FCSTD DOCUMENT  (FreeCAD 0.18R16268 (Git))
Label: asm_Bielle
License: All rights reserved
LicenseURL: http://en.wikipedia.org/wiki/All_rights_reserved
objects: App::Link×5, App::FeaturePython×5, PartDesign::CoordinateSystem×2, App::DocumentObjectGroup×1, App::Part×1
note: 2 computed .brp shape members not serialized (recipe doc carries the construction recipe); baked Part::Feature solids carry a one-line shape summary decoded from their .brp
EXTERNAL_REF file=Bielle.fcstd obj=Model
EXTERNAL_REF file=Cuve.fcstd obj=Model
EXTERNAL_REF file=Bague.fcstd obj=Model
EXTERNAL_REF file=Screw_CHC.fcstd obj=Model

FEATURE [PartDesign::CoordinateSystem] LCS_0
  AttacherType = Attacher::AttachEngine3D
FEATURE [App::Link] Bielle
  LinkedObject = -> <external Bielle.fcstd>#Model
  expr: Placement = <<LCS_0>>.Placement.multiply(<<constr_Bielle>>.AttachmentOffset).multiply(.<<LCS_0.>>.Placement.inverse())
FEATURE [App::FeaturePython] constr_Bielle  # WARN: FeaturePython — macro-defined, semantics opaque (R4)
  AttachedTo = Parent Assembly
  AttachmentLCS = LCS_0
  Link_Name = Bielle
  LinkedPartLCS = LCS_0
  Linked_File = Bielle
FEATURE [App::Link] Cuve
  LinkPlacement = pos=(125,0,0) rot=(0,0,1;0rad)
  LinkedObject = -> <external Cuve.fcstd>#Model
  Placement = pos=(125,0,0) rot=(0,0,1;0rad)
  expr: Placement = <<Bielle>>.Placement.multiply(<<Bielle>>.<<LCS_1.>>.Placement).multiply(<<constr_Cuve>>.AttachmentOffset).multiply(.<<LCS_0.>>.Placement.inverse())
FEATURE [App::FeaturePython] constr_Cuve  # WARN: FeaturePython — macro-defined, semantics opaque (R4)
  AttachedTo = Bielle
  AttachmentLCS = LCS_1
  Link_Name = Cuve
  LinkedPartLCS = LCS_0
  Linked_File = Cuve
FEATURE [App::Link] Bague
  LinkPlacement = pos=(0,0,-15) rot=(0,0,1;0rad)
  LinkedObject = -> <external Bague.fcstd>#Model
  Placement = pos=(0,0,-15) rot=(0,0,1;0rad)
  expr: Placement = <<Bielle>>.Placement.multiply(<<Bielle>>.<<LCS_0.>>.Placement).multiply(<<constr_Bague>>.AttachmentOffset).multiply(.<<LCS_0.>>.Placement.inverse())
FEATURE [App::FeaturePython] constr_Bague  # WARN: FeaturePython — macro-defined, semantics opaque (R4)
  AttachedTo = Bielle
  AttachmentLCS = LCS_0
  AttachmentOffset = pos=(0,0,-15) rot=(0,0,1;0rad)
  Link_Name = Bague
  LinkedPartLCS = LCS_0
  Linked_File = Bague
FEATURE [App::Link] Screw_CHC_1
  LinkPlacement = pos=(130,-32.5,-1.7e-14) rot=(0.707107,0,0.707107;3.14159rad)
  LinkedObject = -> <external Screw_CHC.fcstd>#Model
  Placement = pos=(130,-32.5,-1.7e-14) rot=(0.707107,0,0.707107;3.14159rad)
  expr: Placement = <<Cuve>>.Placement.multiply(<<Cuve>>.<<LCS_1.>>.Placement).multiply(<<constr_Screw_CHC_1>>.AttachmentOffset).multiply(.<<LCS_0.>>.Placement.inverse())
FEATURE [App::FeaturePython] constr_Screw_CHC_1  # WARN: FeaturePython — macro-defined, semantics opaque (R4)
  AttachedTo = Cuve
  AttachmentLCS = LCS_1
  Link_Name = Screw_CHC_1
  LinkedPartLCS = LCS_0
  Linked_File = Screw_CHC
FEATURE [App::Link] Screw_CHC_2
  LinkPlacement = pos=(130,32.5,-2.6e-15) rot=(0.707107,0,0.707107;3.14159rad)
  LinkedObject = -> <external Screw_CHC.fcstd>#Model
  Placement = pos=(130,32.5,-2.6e-15) rot=(0.707107,0,0.707107;3.14159rad)
  expr: Placement = <<Cuve>>.Placement.multiply(<<Cuve>>.<<LCS_2.>>.Placement).multiply(<<constr_Screw_CHC_2>>.AttachmentOffset).multiply(.<<LCS_0.>>.Placement.inverse())
FEATURE [App::FeaturePython] constr_Screw_CHC_2  # WARN: FeaturePython — macro-defined, semantics opaque (R4)
  AttachedTo = Cuve
  AttachmentLCS = LCS_2
  Link_Name = Screw_CHC_2
  LinkedPartLCS = LCS_0
  Linked_File = Screw_CHC
FEATURE [App::DocumentObjectGroup] Constraints
  Group = -> [constr_Bielle,constr_Cuve,constr_Bague,constr_Screw_CHC_1,constr_Screw_CHC_2]
FEATURE [PartDesign::CoordinateSystem] LCS_Cuve
  AttacherType = Attacher::AttachEngine3D
  Placement = pos=(125,0,0) rot=(0,0,1;0rad)
  expr: Placement = <<Cuve>>.Placement.multiply(<<Cuve>>.<<LCS_0.>>.Placement)
FEATURE [App::Part] Model
  Group = -> [Constraints,LCS_0,Bielle,constr_Bielle,Cuve,constr_Cuve,Bague,constr_Bague,Screw_CHC_1,constr_Screw_CHC_1,Screw_CHC_2,constr_Screw_CHC_2,LCS_Cuve]
  Origin = -> Origin

RESOLVED EXTERNAL PARTS (link-assembly join: the EXTERNAL_REF files above that resolve inside this repo's crawl, each included once):
---- part Bague.fcstd = doc fcstd_d0fe9226a57d ----
FCSTD DOCUMENT  (FreeCAD 0.18R16268 (Git))
Label: Bague
License: All rights reserved
LicenseURL: http://en.wikipedia.org/wiki/All_rights_reserved
objects: PartDesign::CoordinateSystem×3, App::DocumentObjectGroup×1, Sketcher::SketchObject×1, PartDesign::Pad×1, PartDesign::Chamfer×1, PartDesign::Body×1, App::Part×1
note: 8 computed .brp shape members not serialized (recipe doc carries the construction recipe); baked Part::Feature solids carry a one-line shape summary decoded from their .brp

FEATURE [App::DocumentObjectGroup] Constraints
FEATURE [PartDesign::CoordinateSystem] LCS_0
  AttacherType = Attacher::AttachEngine3D
FEATURE [PartDesign::CoordinateSystem] LCS_001
  AttacherType = Attacher::AttachEngine3D
FEATURE [Sketcher::SketchObject] Sketch
  MapMode = 5
  Support = -> [XY_Plane001]
  sketch-geometry (2):
    g0: Circle CenterX=0 CenterY=0 CenterZ=0 NormalX=0 NormalY=0 NormalZ=1 AngleXU=0 Radius=8
    g1: Circle CenterX=0 CenterY=0 CenterZ=0 NormalX=0 NormalY=0 NormalZ=1 AngleXU=0 Radius=10
  constraints (4):
    c: Coincident(g0,g-1)
    c: Coincident(g1,g0)
    c: Diameter(g1) = 20
    c: Diameter(g0) = 16
FEATURE [PartDesign::Pad] Pad
  ClaimChildren = false
  Length = 30
  Length2 = 100
  Profile = -> Sketch
  Type = 0
FEATURE [PartDesign::Chamfer] Chamfer
  Base = -> Pad [Face4,Face3]
  BaseFeature = -> Pad
  Size = 0.5
FEATURE [PartDesign::Body] Body
  Group = -> [LCS_001,Sketch,Pad,Chamfer]
  Origin = -> Origin001
  Tip = -> Chamfer
FEATURE [PartDesign::CoordinateSystem] LCS_1
  AttacherType = Attacher::AttachEngine3D
  AttachmentOffset = pos=(0,0,0) rot=(0,0,-1;1.5708rad)
  MapMode = 11
  Placement = pos=(0,0,30) rot=(0,0,1;0rad)
  Support = -> [Pad]
FEATURE [App::Part] Model
  Group = -> [Constraints,LCS_0,Body,LCS_1]
  Origin = -> Origin
---- part Bielle.fcstd = doc fcstd_74266f76e503 ----
FCSTD DOCUMENT  (FreeCAD 0.18R16268 (Git))
Label: Bielle
License: All rights reserved
LicenseURL: http://en.wikipedia.org/wiki/All_rights_reserved
objects: Sketcher::SketchObject×6, PartDesign::Pad×3, PartDesign::CoordinateSystem×2, PartDesign::Plane×2, PartDesign::Pocket×2, App::DocumentObjectGroup×1, PartDesign::Mirrored×1, PartDesign::Body×1, App::Part×1
note: 22 computed .brp shape members not serialized (recipe doc carries the construction recipe); baked Part::Feature solids carry a one-line shape summary decoded from their .brp

FEATURE [App::DocumentObjectGroup] Constraints
FEATURE [PartDesign::CoordinateSystem] LCS_0
  AttacherType = Attacher::AttachEngine3D
FEATURE [PartDesign::Plane] DatumPlane
  AttachmentOffset = pos=(0,0,1.5) rot=(0,0,1;0rad)
  Length = 161.166
  MapMode = 5
  Placement = pos=(0,0,1.5) rot=(0,0,1;0rad)
  ResizeMode = 0
  Support = -> [LCS_0]
  Width = 101.166
FEATURE [Sketcher::SketchObject] Sketch  label="Length"
  MapMode = 5
  Support = -> [XY_Plane001]
  sketch-geometry (1):
    g0: LineSegment StartX=0 StartY=0 StartZ=0 EndX=125 EndY=0 EndZ=0
  constraints (3):
    c: Horizontal(g0)
    c: DistanceX(g0,g0) = 125
    c: Coincident(g-1,g0)
FEATURE [PartDesign::Plane] DatumPlane001
  Length = 88.9443
  MapMode = 7
  Placement = pos=(125,0,0) rot=(0.57735,-0.57735,-0.57735;2.0944rad)
  ResizeMode = 0
  Support = -> [Sketch]
  Width = 33.9443
FEATURE [Sketcher::SketchObject] Sketch006
  MapMode = 5
  Placement = pos=(125,0,0) rot=(0.57735,-0.57735,-0.57735;2.0944rad)
  Support = -> [DatumPlane001]
  sketch-geometry (2):
    g0: Circle CenterX=-32.5 CenterY=0 CenterZ=0 NormalX=0 NormalY=0 NormalZ=1 AngleXU=0 Radius=2.5
    g1: Circle CenterX=32.5 CenterY=0 CenterZ=0 NormalX=0 NormalY=0 NormalZ=1 AngleXU=0 Radius=2.5
  constraints (5):
    c: Symmetric(g0,g1,g-2)
    c: PointOnObject(g1,g-1)
    c: Equal(g0,g1)
    c: Diameter(g0) = 5
    c: DistanceX(g0,g1) = 65
FEATURE [Sketcher::SketchObject] Sketch001
  MapMode = 5
  Support = -> [XY_Plane001]
  sketch-geometry (2):
    g0: Circle CenterX=0 CenterY=0 CenterZ=0 NormalX=0 NormalY=0 NormalZ=1 AngleXU=0 Radius=10
    g1: Circle CenterX=0 CenterY=0 CenterZ=0 NormalX=0 NormalY=0 NormalZ=1 AngleXU=0 Radius=15
  constraints (4):
    c: Coincident(g0,g-1)
    c: Diameter(g0) = 20
    c: Diameter(g1) = 30
    c: Coincident(g1,g0)
FEATURE [PartDesign::Pad] Pad
  ClaimChildren = false
  Length = 25
  Length2 = 100
  Midplane = true
  Profile = -> Sketch001
  Type = 0
FEATURE [Sketcher::SketchObject] Sketch003
  ExternalGeometry = -> [Sketch]
  MapMode = 5
  Support = -> [XY_Plane001]
  sketch-geometry (4):
    g0: ArcOfCircle CenterX=125 CenterY=0 CenterZ=0 NormalX=0 NormalY=0 NormalZ=1 AngleXU=0 Radius=20 StartAngle=1.5708 EndAngle=4.71239
    g1: ArcOfCircle CenterX=125 CenterY=0 CenterZ=0 NormalX=0 NormalY=0 NormalZ=1 AngleXU=0 Radius=25 StartAngle=1.5708 EndAngle=4.71239
    g2: LineSegment StartX=125 StartY=25 StartZ=0 EndX=125 EndY=20 EndZ=0
    g3: LineSegment StartX=125 StartY=-20 StartZ=0 EndX=125 EndY=-25 EndZ=0
  constraints (12):
    c: Coincident(g0,g-3)
    c: Coincident(g1,g0)
    c: Coincident(g2,g1)
    c: Coincident(g2,g0)
    c: Coincident(g3,g0)
    c: Coincident(g3,g1)
    c: Vertical(g2)
    c: Vertical(g3)
    c: PointOnObject(g0,g2)
    c: PointOnObject(g0,g3)
    c: DistanceY(g2,g2) = 5
    c: Diameter(g0) = 40
FEATURE [Sketcher::SketchObject] Sketch004
  ExternalGeometry = -> [Sketch001,Sketch003]
  MapMode = 5
  Support = -> [XY_Plane001]
  sketch-geometry (10):
    g0: LineSegment StartX=125 StartY=25 StartZ=0 EndX=125 EndY=40 EndZ=0
    g1: LineSegment StartX=125 StartY=40 StartZ=0 EndX=115 EndY=40 EndZ=0
    g2: LineSegment StartX=115 StartY=40 StartZ=0 EndX=95 EndY=20 EndZ=0
    g3: LineSegment StartX=95 StartY=20 StartZ=0 EndX=11.1803 EndY=10 EndZ=0
    g4: LineSegment StartX=11.1803 StartY=-10 StartZ=0 EndX=95 EndY=-20 EndZ=0
    g5: LineSegment StartX=95 StartY=-20 StartZ=0 EndX=115 EndY=-40 EndZ=0
    g6: LineSegment StartX=115 StartY=-40 StartZ=0 EndX=125 EndY=-40 EndZ=0
    g7: LineSegment StartX=125 StartY=-40 StartZ=0 EndX=125 EndY=-25 EndZ=0
    g8: ArcOfCircle CenterX=125 CenterY=8e-16 CenterZ=0 NormalX=0 NormalY=0 NormalZ=1 AngleXU=0 Radius=25 StartAngle=1.5708 EndAngle=4.71239
    g9: ArcOfCircle CenterX=0 CenterY=-9e-16 CenterZ=0 NormalX=0 NormalY=0 NormalZ=1 AngleXU=0 Radius=15 StartAngle=5.55346 EndAngle=7.01291
  constraints (27):
    c: Coincident(g0,g1)
    c: Coincident(g1,g2)
    c: Coincident(g2,g3)
    c: PointOnObject(g3,g-3)
    c: Coincident(g4,g5)
    c: Coincident(g5,g6)
    c: Coincident(g6,g7)
    c: Coincident(g7,g-4)
    c: Vertical(g0)
    c: Symmetric(g3,g4,g-1)
    c: DistanceY(g4,g2) = 40
    c: Symmetric(g2,g4,g-1)
    c: Horizontal(g1)
    c: DistanceY(g6,g0) = 80
    c: Symmetric(g0,g6,g-1)
    c: Symmetric(g1,g5,g-1)
    c: DistanceX(g1,g1) = 10
    c: Angle(g2,g1) = 2.35619
    c: DistanceY(g4,g3) = 20
    c: Coincident(g8,g7)
    c: Coincident(g9,g3)
    c: Coincident(g9,g4)
    c: Coincident(g9,g-1)
    c: Parallel(g7,g0)
    c: Coincident(g0,g8)
    c: PointOnObject(g0,g-5)
    c: PointOnObject(g8,g7)
FEATURE [Sketcher::SketchObject] Sketch005
  ExternalGeometry = -> [Sketch004,Sketch001,Sketch003]
  MapMode = 5
  Placement = pos=(0,0,1.5) rot=(0,0,1;0rad)
  Support = -> [DatumPlane]
  sketch-geometry (8):
    g0: ArcOfCircle CenterX=26.7773 CenterY=0 CenterZ=0 NormalX=0 NormalY=0 NormalZ=1 AngleXU=0 Radius=8.77725 StartAngle=1.68954 EndAngle=4.59365
    g1: ArcOfCircle CenterX=79.9265 CenterY=0 CenterZ=0 NormalX=0 NormalY=0 NormalZ=1 AngleXU=0 Radius=15.0735 StartAngle=4.59365 EndAngle=7.97272
    g2: LineSegment StartX=25.7375 StartY=8.71545 StartZ=0 EndX=78.1408 EndY=14.9674 EndZ=0
    g3: LineSegment StartX=25.7375 StartY=-8.71545 StartZ=0 EndX=78.1408 EndY=-14.9674 EndZ=0
    g4: GeomPoint X=18 Y=0 Z=0
    g5: GeomPoint X=15 Y=0 Z=0
    g6: GeomPoint X=95 Y=0 Z=0
    g7: GeomPoint X=100 Y=0 Z=0
  constraints (18):
    c: PointOnObject(g0,g-1)
    c: PointOnObject(g1,g-1)
    c: Tangent(g2,g1) = 1.5708
    c: Tangent(g3,g1) = -1.5708
    c: Tangent(g2,g0) = 1.5708
    c: Tangent(g3,g0) = -1.5708
    c: PointOnObject(g5,g-4)
    c: Horizontal(g5,g0)
    c: Horizontal(g4,g0)
    c: PointOnObject(g4,g0)
    c: PointOnObject(g6,g1)
    c: Horizontal(g6,g1)
    c: Parallel(g2,g-5)
    c: Distance(g5,g4) = 3
    c: Distance(g0,g-5) = 3
    c: PointOnObject(g7,g-6)
    c: PointOnObject(g7,g-1)
    c: DistanceX(g6,g7) = 5
FEATURE [PartDesign::Pad] Pad001
  BaseFeature = -> Pad
  ClaimChildren = false
  Length = 20
  Length2 = 100
  Midplane = true
  Profile = -> Sketch004
  Type = 0
FEATURE [PartDesign::Pad] Pad002
  BaseFeature = -> Pad001
  ClaimChildren = false
  Length = 25
  Length2 = 100
  Midplane = true
  Profile = -> Sketch003
  Type = 0
FEATURE [PartDesign::Pocket] Pocket
  BaseFeature = -> Pad002
  ClaimChildren = false
  Length = 5
  Length2 = 100
  Profile = -> Sketch005
  Reversed = true
  Type = 1
FEATURE [PartDesign::Mirrored] Mirrored
  BaseFeature = -> Pocket
  MirrorPlane = -> XY_Plane001
  Originals = -> [Pocket]
FEATURE [PartDesign::Pocket] Pocket001
  BaseFeature = -> Mirrored
  ClaimChildren = false
  Length = 5
  Length2 = 100
  Profile = -> Sketch006
  Reversed = true
  Type = 1
FEATURE [PartDesign::Body] Body
  Group = -> [Sketch,Sketch001,Sketch003,Sketch004,DatumPlane001,DatumPlane,Sketch005,Pad,Pad001,Pad002,Pocket,Mirrored,Sketch006,Pocket001]
  Origin = -> Origin001
  Tip = -> Pocket001
FEATURE [PartDesign::CoordinateSystem] LCS_1
  AttacherType = Attacher::AttachEngine3D
  MapMode = 1
  Placement = pos=(125,0,0) rot=(0,0,1;0rad)
  Support = -> [Sketch]
FEATURE [App::Part] Model
  Group = -> [Constraints,LCS_0,Body,LCS_1]
  Origin = -> Origin
---- part Cuve.fcstd = doc fcstd_13ffda280443 ----
FCSTD DOCUMENT  (FreeCAD 0.18R16268 (Git))
Label: Cuve
License: All rights reserved
LicenseURL: http://en.wikipedia.org/wiki/All_rights_reserved
objects: PartDesign::CoordinateSystem×4, Sketcher::SketchObject×4, PartDesign::Pad×2, PartDesign::Pocket×2, App::DocumentObjectGroup×1, PartDesign::Plane×1, PartDesign::Mirrored×1, PartDesign::Body×1, App::Part×1
note: 19 computed .brp shape members not serialized (recipe doc carries the construction recipe); baked Part::Feature solids carry a one-line shape summary decoded from their .brp

FEATURE [App::DocumentObjectGroup] Constraints
FEATURE [PartDesign::CoordinateSystem] LCS_0
  AttacherType = Attacher::AttachEngine3D
FEATURE [PartDesign::CoordinateSystem] LCS_001
  AttacherType = Attacher::AttachEngine3D
FEATURE [Sketcher::SketchObject] Sketch
  MapMode = 5
  Support = -> [XY_Plane001]
  sketch-geometry (4):
    g0: ArcOfCircle CenterX=0 CenterY=0 CenterZ=0 NormalX=0 NormalY=0 NormalZ=1 AngleXU=0 Radius=20 StartAngle=4.71239 EndAngle=7.85398
    g1: ArcOfCircle CenterX=0 CenterY=0 CenterZ=0 NormalX=0 NormalY=0 NormalZ=1 AngleXU=0 Radius=25 StartAngle=4.71239 EndAngle=7.85398
    g2: LineSegment StartX=7.7e-15 StartY=25 StartZ=0 EndX=7.7e-15 EndY=20 EndZ=0
    g3: LineSegment StartX=-3.7e-15 StartY=-20 StartZ=0 EndX=-3.7e-15 EndY=-25 EndZ=0
  constraints (12):
    c: Coincident(g0,g-1)
    c: Coincident(g1,g0)
    c: Vertical(g2)
    c: Vertical(g3)
    c: PointOnObject(g0,g3)
    c: Coincident(g0,g3)
    c: Coincident(g0,g2)
    c: Coincident(g1,g3)
    c: Coincident(g1,g2)
    c: PointOnObject(g0,g3)
    c: Diameter(g0) = 40
    c: DistanceY(g2,g2) = 5
FEATURE [PartDesign::Pad] Pad
  ClaimChildren = false
  Length = 25
  Length2 = 100
  Midplane = true
  Profile = -> Sketch
  Type = 0
FEATURE [Sketcher::SketchObject] Sketch001
  ExternalGeometry = -> [Sketch]
  MapMode = 5
  Support = -> [XY_Plane001]
  sketch-geometry (9):
    g0: LineSegment StartX=0 StartY=25 StartZ=0 EndX=0 EndY=40 EndZ=0
    g1: LineSegment StartX=0 StartY=40 StartZ=0 EndX=10 EndY=40 EndZ=0
    g2: LineSegment StartX=10 StartY=40 StartZ=0 EndX=28 EndY=22 EndZ=0
    g3: LineSegment StartX=28 StartY=22 StartZ=0 EndX=28 EndY=-22 EndZ=0
    g4: LineSegment StartX=28 StartY=-22 StartZ=0 EndX=10 EndY=-40 EndZ=0
    g5: LineSegment StartX=10 StartY=-40 StartZ=0 EndX=0 EndY=-40 EndZ=0
    g6: LineSegment StartX=0 StartY=-40 StartZ=0 EndX=0 EndY=-25 EndZ=0
    g7: ArcOfCircle CenterX=0 CenterY=0 CenterZ=0 NormalX=0 NormalY=0 NormalZ=1 AngleXU=0 Radius=25 StartAngle=4.71239 EndAngle=7.85398
    g8: GeomPoint X=25 Y=0 Z=0
  constraints (23):
    c: Coincident(g0,g1)
    c: Horizontal(g1)
    c: Coincident(g1,g2)
    c: Coincident(g2,g3)
    c: Coincident(g3,g4)
    c: Coincident(g4,g5)
    c: PointOnObject(g5,g-2)
    c: Coincident(g5,g6)
    c: Symmetric(g0,g5,g-1)
    c: Symmetric(g2,g3,g-1)
    c: Symmetric(g1,g4,g-1)
    c: Distance(g0,g5) = 80
    c: DistanceX(g1,g1) = 10
    c: PointOnObject(g8,g-1)
    c: PointOnObject(g8,g7)
    c: Distance(g8,g3) = 3
    c: Angle(g1,g2) = 2.35619
    c: Coincident(g6,g7)
    c: Coincident(g7,g0)
    c: Vertical(g0)
    c: Vertical(g6)
    c: Coincident(g7,g-1)
    c: Equal(g-3,g7)
FEATURE [PartDesign::Pad] Pad001
  BaseFeature = -> Pad
  ClaimChildren = false
  Length = 20
  Length2 = 100
  Midplane = true
  Profile = -> Sketch001
  Type = 0
FEATURE [PartDesign::Plane] DatumPlane
  AttachmentOffset = pos=(0,0,5) rot=(0,0,1;0rad)
  Length = 88.9443
  MapMode = 5
  Placement = pos=(5,-1.1e-15,1.1e-15) rot=(0.57735,0.57735,0.57735;2.0944rad)
  ResizeMode = 0
  Support = -> [YZ_Plane001]
  Width = 33.9443
FEATURE [Sketcher::SketchObject] Sketch002
  MapMode = 5
  Placement = pos=(5,-1.1e-15,1.1e-15) rot=(0.57735,0.57735,0.57735;2.0944rad)
  Support = -> [DatumPlane]
  sketch-geometry (4):
    g0: ArcOfCircle CenterX=32.5 CenterY=0 CenterZ=0 NormalX=0 NormalY=0 NormalZ=1 AngleXU=0 Radius=6 StartAngle=1.5708 EndAngle=4.71239
    g1: LineSegment StartX=32.5 StartY=6 StartZ=0 EndX=113.901 EndY=6 EndZ=0
    g2: LineSegment StartX=113.901 StartY=6 StartZ=0 EndX=113.901 EndY=-6 EndZ=0
    g3: LineSegment StartX=113.901 StartY=-6 StartZ=0 EndX=32.5 EndY=-6 EndZ=0
  constraints (10):
    c: Tangent(g0,g1) = 1.5708
    c: Coincident(g1,g2)
    c: Vertical(g2)
    c: Coincident(g2,g3)
    c: Tangent(g3,g0) = 1.5708
    c: Horizontal(g3)
    c: Horizontal(g1)
    c: PointOnObject(g0,g-1)
    c: DistanceY(g2,g2) = 12
    c: DistanceX(g-1,g0) = 32.5
FEATURE [PartDesign::Pocket] Pocket
  BaseFeature = -> Pad001
  ClaimChildren = false
  Length = 5
  Length2 = 100
  Profile = -> Sketch002
  Reversed = true
  Type = 1
FEATURE [PartDesign::Mirrored] Mirrored
  BaseFeature = -> Pocket
  MirrorPlane = -> XZ_Plane001
  Originals = -> [Pocket]
FEATURE [Sketcher::SketchObject] Sketch003
  ExternalGeometry = -> [Mirrored]
  MapMode = 5
  Placement = pos=(5,-1.1e-15,1.1e-15) rot=(0.57735,0.57735,0.57735;2.0944rad)
  Support = -> [DatumPlane]
  sketch-geometry (2):
    g0: Circle CenterX=32.5 CenterY=-3.6e-15 CenterZ=0 NormalX=0 NormalY=0 NormalZ=1 AngleXU=0 Radius=3.25
    g1: Circle CenterX=-32.5 CenterY=-1.8e-14 CenterZ=0 NormalX=0 NormalY=0 NormalZ=1 AngleXU=0 Radius=3.25
  constraints (4):
    c: Coincident(g0,g-4)
    c: Coincident(g1,g-3)
    c: Equal(g1,g0)
    c: Diameter(g0) = 6.5
FEATURE [PartDesign::Pocket] Pocket001
  BaseFeature = -> Mirrored
  ClaimChildren = false
  Length = 10
  Length2 = 100
  Profile = -> Sketch003
  Type = 0
FEATURE [PartDesign::Body] Body
  Group = -> [LCS_001,Sketch,Pad,Sketch001,Pad001,DatumPlane,Sketch002,Pocket,Mirrored,Sketch003,Pocket001]
  Origin = -> Origin001
  Tip = -> Pocket001
FEATURE [PartDesign::CoordinateSystem] LCS_1
  AttacherType = Attacher::AttachEngine3D
  MapMode = 11
  Placement = pos=(5,-32.5,-1.7e-14) rot=(0.707107,0,0.707107;3.14159rad)
  Support = -> [Pocket001]
FEATURE [PartDesign::CoordinateSystem] LCS_2
  AttacherType = Attacher::AttachEngine3D
  MapMode = 11
  Placement = pos=(5,32.5,-2.6e-15) rot=(0.707107,0,0.707107;3.14159rad)
  Support = -> [Pocket001]
FEATURE [App::Part] Model
  Group = -> [Constraints,LCS_0,Body,LCS_1,LCS_2]
  Origin = -> Origin
---- part Screw_CHC.fcstd = doc fcstd_0d870e337e92 ----
FCSTD DOCUMENT  (FreeCAD 0.18R16268 (Git))
Label: Screw_CHC
License: All rights reserved
LicenseURL: http://en.wikipedia.org/wiki/All_rights_reserved
objects: Sketcher::SketchObject×3, PartDesign::CoordinateSystem×2, PartDesign::Pad×2, App::DocumentObjectGroup×1, PartDesign::Pocket×1, PartDesign::Fillet×1, PartDesign::Chamfer×1, PartDesign::Body×1, App::Part×1
note: 14 computed .brp shape members not serialized (recipe doc carries the construction recipe); baked Part::Feature solids carry a one-line shape summary decoded from their .brp

FEATURE [App::DocumentObjectGroup] Constraints
FEATURE [PartDesign::CoordinateSystem] LCS_0
  AttacherType = Attacher::AttachEngine3D
FEATURE [PartDesign::CoordinateSystem] LCS_001
  AttacherType = Attacher::AttachEngine3D
FEATURE [Sketcher::SketchObject] Sketch
  MapMode = 5
  Support = -> [XY_Plane001]
  sketch-geometry (1):
    g0: Circle CenterX=0 CenterY=0 CenterZ=0 NormalX=0 NormalY=0 NormalZ=1 AngleXU=0 Radius=5
  constraints (2):
    c: Coincident(g0,g-1)
    c: Diameter(g0) = 10
FEATURE [PartDesign::Pad] Pad
  ClaimChildren = false
  Length = 6
  Length2 = 100
  Profile = -> Sketch
  Type = 0
FEATURE [Sketcher::SketchObject] Sketch001
  MapMode = 5
  Placement = pos=(0,0,6) rot=(0,0,1;0rad)
  Support = -> [Pad]
  sketch-geometry (7):
    g0: LineSegment StartX=2.88675 StartY=0 StartZ=0 EndX=1.44338 EndY=2.5 EndZ=0
    g1: LineSegment StartX=1.44338 StartY=2.5 StartZ=0 EndX=-1.44338 EndY=2.5 EndZ=0
    g2: LineSegment StartX=-1.44338 StartY=2.5 StartZ=0 EndX=-2.88675 EndY=8.48e-14 EndZ=0
    g3: LineSegment StartX=-2.88675 StartY=8.48e-14 StartZ=0 EndX=-1.44338 EndY=-2.5 EndZ=0
    g4: LineSegment StartX=-1.44338 StartY=-2.5 StartZ=0 EndX=1.44338 EndY=-2.5 EndZ=0
    g5: LineSegment StartX=1.44338 StartY=-2.5 StartZ=0 EndX=2.88675 EndY=0 EndZ=0
    g6: Circle [constr] CenterX=0 CenterY=0 CenterZ=0 NormalX=0 NormalY=0 NormalZ=1 AngleXU=0 Radius=2.88675
  constraints (16):
    c: Coincident(g0,g1)
    c: Coincident(g1,g2)
    c: Coincident(g2,g3)
    c: Coincident(g3,g4)
    c: Coincident(g4,g5)
    c: Coincident(g5,g0)
    c: Equal(g0, g1-g5) x5
    c: PointOnObject(g0,g6)
    c: PointOnObject(g1,g6)
    c: PointOnObject(g2,g6)
    c: PointOnObject(g3,g6)
    c: PointOnObject(g4,g6)
    c: PointOnObject(g5,g6)
    c: Coincident(g6,g-1)
    c: PointOnObject(g5,g-1)
    c: Distance(g0,g4) = 5
FEATURE [PartDesign::Pocket] Pocket
  BaseFeature = -> Pad
  ClaimChildren = false
  Length = 4
  Length2 = 100
  Profile = -> Sketch001
  Type = 0
FEATURE [Sketcher::SketchObject] Sketch002
  MapMode = 5
  Support = -> [XY_Plane001]
  sketch-geometry (1):
    g0: Circle CenterX=0 CenterY=0 CenterZ=0 NormalX=0 NormalY=0 NormalZ=1 AngleXU=0 Radius=3
  constraints (2):
    c: Coincident(g0,g-1)
    c: Diameter(g0) = 6
FEATURE [PartDesign::Pad] Pad001
  BaseFeature = -> Pocket
  ClaimChildren = false
  Length = 20
  Length2 = 100
  Profile = -> Sketch002
  Reversed = true
  Type = 0
FEATURE [PartDesign::Fillet] Fillet
  Base = -> Pad001 [Edge3]
  BaseFeature = -> Pad001
  Radius = 0.5
FEATURE [PartDesign::Chamfer] Chamfer
  Base = -> Fillet [Face12]
  BaseFeature = -> Fillet
  Size = 0.5
FEATURE [PartDesign::Body] Body
  Group = -> [LCS_001,Sketch,Pad,Sketch001,Pocket,Sketch002,Pad001,Fillet,Chamfer]
  Origin = -> Origin001
  Tip = -> Chamfer
FEATURE [App::Part] Model
  Group = -> [Constraints,LCS_0,Body]
  Origin = -> Origin
